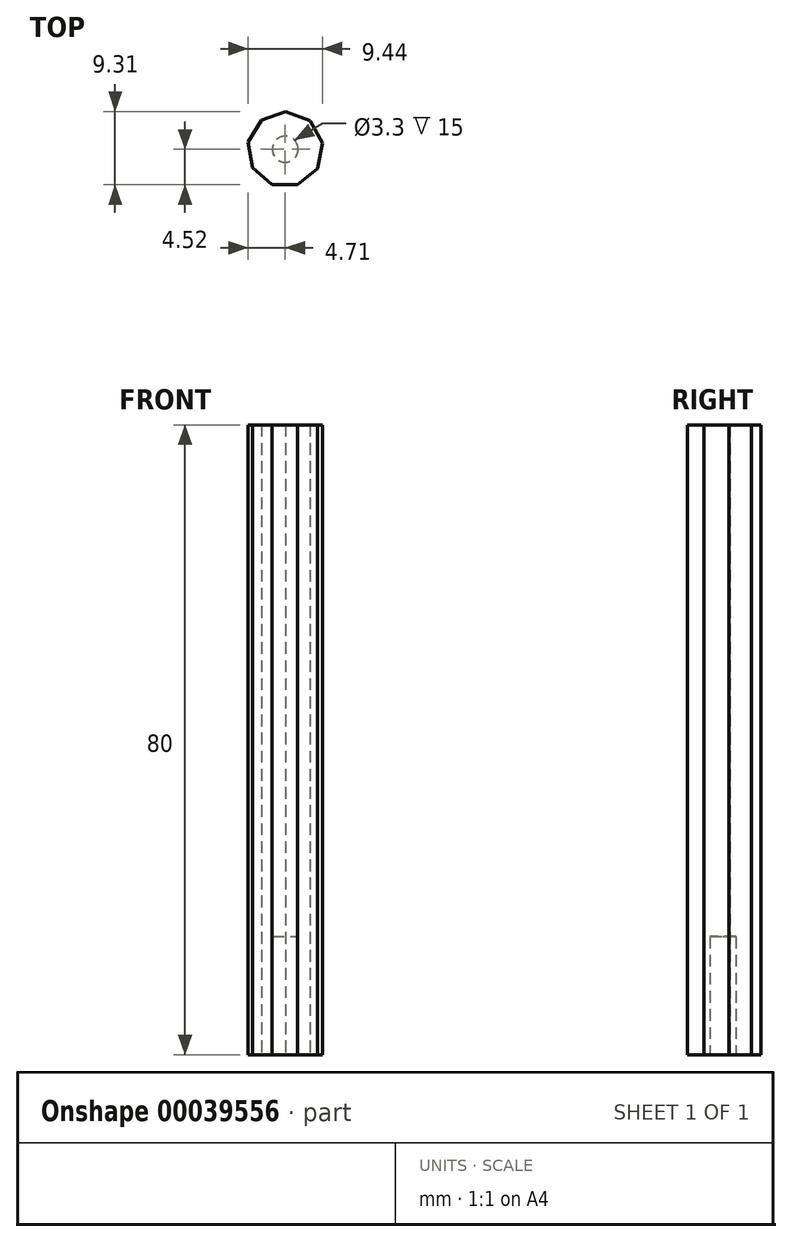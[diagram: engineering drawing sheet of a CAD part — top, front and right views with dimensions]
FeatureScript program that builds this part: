
annotation { "Feature Type Name" : "Feature", "Feature Type Description" : "" }
export const myFeature = defineFeature(function(context is Context, id is Id, definition is map)
    precondition{}
    {
        {
            var Q0;
            Q0=qCreatedBy(makeId("Top.planeOp"),FACE);
            var sketch = newSketch(context, id + "F0", { "sketchPlane" : qUnion([Q0])});
            skCircle(sketch, "E0.cCircle", {"center": v(0, 0) * mm, "radius": 4.5 * mm, "construction": true});
            skLineSegment(sketch, "E0.0", {"start": v(3.12, 3.63) * mm, "end": v(4.73, 0.78) * mm});
            skLineSegment(sketch, "E0.1", {"start": v(4.73, 0.78) * mm, "end": v(4.12, -2.44) * mm});
            skLineSegment(sketch, "E0.2", {"start": v(4.12, -2.44) * mm, "end": v(1.58, -4.52) * mm});
            skLineSegment(sketch, "E0.3", {"start": v(1.58, -4.52) * mm, "end": v(-1.7, -4.48) * mm});
            skLineSegment(sketch, "E0.4", {"start": v(-1.7, -4.48) * mm, "end": v(-4.18, -2.35) * mm});
            skLineSegment(sketch, "E0.5", {"start": v(-4.18, -2.35) * mm, "end": v(-4.7, 0.89) * mm});
            skLineSegment(sketch, "E0.6", {"start": v(-4.7, 0.89) * mm, "end": v(-3.03, 3.7) * mm});
            skLineSegment(sketch, "E0.7", {"start": v(-3.03, 3.7) * mm, "end": v(0.06, 4.79) * mm});
            skLineSegment(sketch, "E0.8", {"start": v(0.06, 4.79) * mm, "end": v(3.12, 3.63) * mm});
            skPoint(sketch, "E0.0.midPoint", {"position": v(3.92, 2.2) * mm});
            skSolve(sketch);
        }
        {
            var Q0;
            Q0 = qSketchRegion(id + "F0", true);
            extrude(context, id + "F1", {"entities" : qUnion([Q0]), "depth" : 80 * mm});
        }
        {
            var Q0;
            Q0=makeQuery(id+"F1.opExtrude","CAP_FACE",FACE,{"disambiguationData":[OSD([sQuery(id+"F0.wireOp",EDGE,"E0.0"),sQuery(id+"F0.wireOp",EDGE,"E0.1"),sQuery(id+"F0.wireOp",EDGE,"E0.2"),sQuery(id+"F0.wireOp",EDGE,"E0.3"),sQuery(id+"F0.wireOp",EDGE,"E0.4"),sQuery(id+"F0.wireOp",EDGE,"E0.5"),sQuery(id+"F0.wireOp",EDGE,"E0.6"),sQuery(id+"F0.wireOp",EDGE,"E0.7"),sQuery(id+"F0.wireOp",EDGE,"E0.8")])],"isStart":true});
            var sketch = newSketch(context, id + "F2", { "sketchPlane" : qUnion([Q0])});
            skCircle(sketch, "E1", {"center": v(0, 0) * mm, "radius": 1.65 * mm});
            skSolve(sketch);
        }
        {
            var Q0;
            Q0=makeQuery(id+"F2.imprint","IMPRINT",FACE,{"disambiguationData":[TD([[makeQuery(id+"F2.imprint","IMPRINT",EDGE,{"derivedFrom":sQuery(id+"F2.wireOp",EDGE,"E1")}),1.0]])]});
            extrude(context, id + "F3", {"entities" : qUnion([Q0]), "operationType" : NewBodyOperationType.REMOVE, "oppositeDirection" : true, "depth" : 15 * mm});
        }
    });
